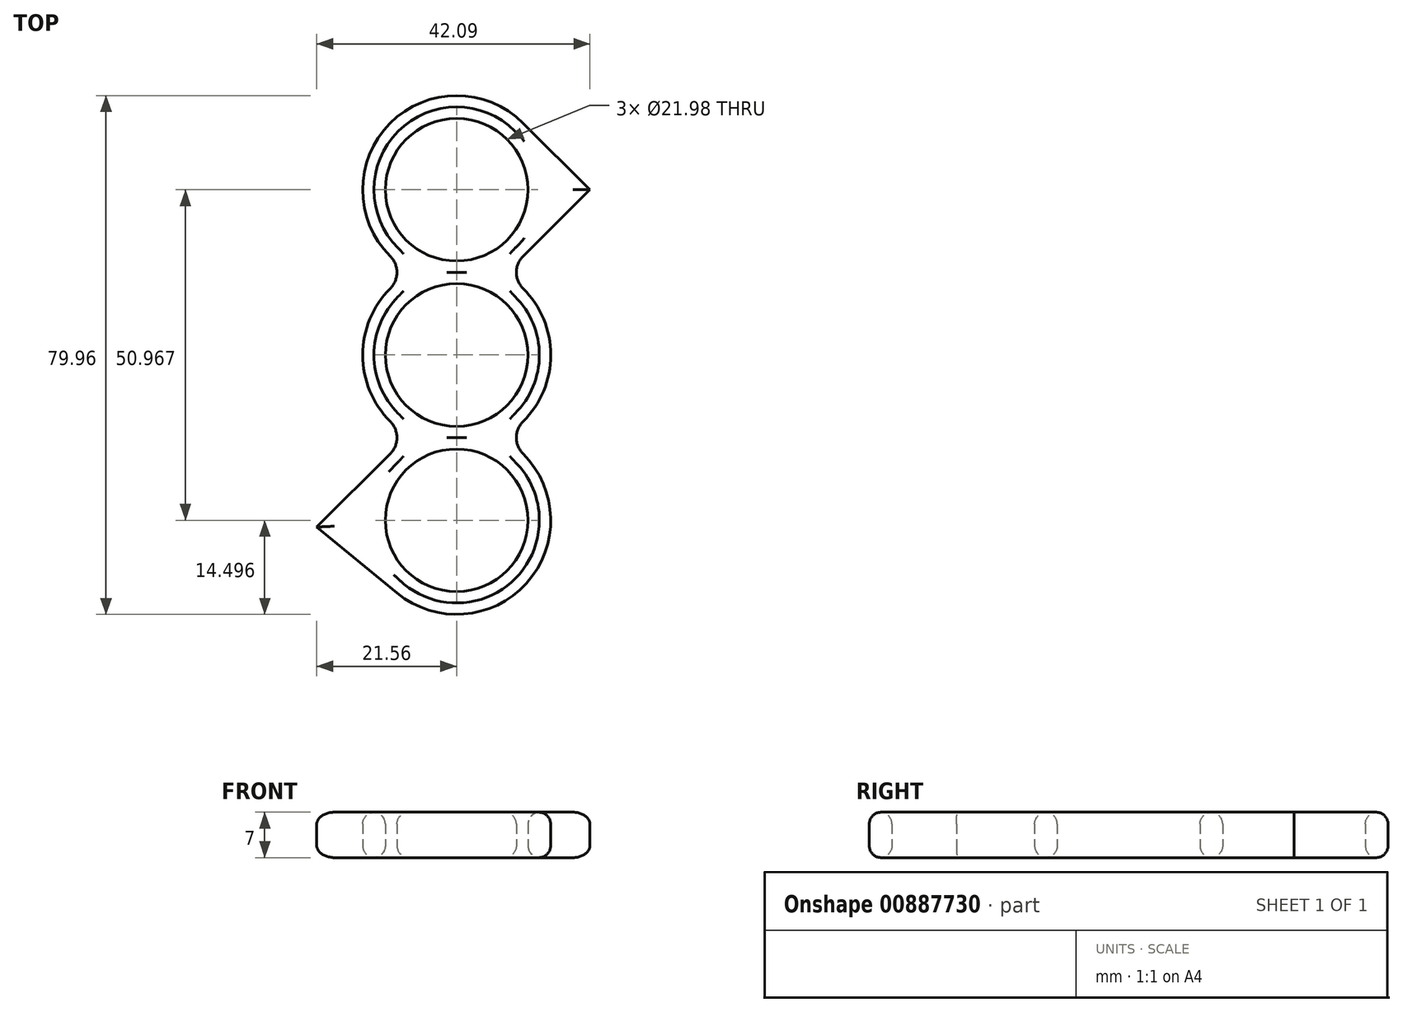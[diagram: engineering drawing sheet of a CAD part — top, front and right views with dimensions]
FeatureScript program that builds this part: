
annotation { "Feature Type Name" : "Feature", "Feature Type Description" : "" }
export const myFeature = defineFeature(function(context is Context, id is Id, definition is map)
    precondition{}
    {
        {
            var Q0;
            Q0=qCreatedBy(makeId("Top.planeOp"),FACE);
            var sketch = newSketch(context, id + "F0", { "sketchPlane" : qUnion([Q0])});
            skCircle(sketch, "E0", {"center": v(0, 0) * mm, "radius": 11 * mm});
            skCircle(sketch, "E1", {"center": v(0, 25.48) * mm, "radius": 11 * mm});
            skCircle(sketch, "E2", {"center": v(0, -25.48) * mm, "radius": 11 * mm});
            skLineSegment(sketch, "E3", {"start": v(0, 25.48) * mm, "end": v(0, -25.48) * mm, "construction": true});
            skLineSegment(sketch, "E4.bottom", {"start": v(-29.85, 57.15) * mm, "end": v(29.85, 57.15) * mm, "construction": true});
            skLineSegment(sketch, "E4.top", {"start": v(-29.85, -57.15) * mm, "end": v(29.85, -57.15) * mm, "construction": true});
            skLineSegment(sketch, "E4.left", {"start": v(-29.84, 57.15) * mm, "end": v(-29.85, -57.15) * mm, "construction": true});
            skLineSegment(sketch, "E4.right", {"start": v(29.85, 57.15) * mm, "end": v(29.84, -57.15) * mm, "construction": true});
            skPoint(sketch, "E5", {"position": v(0, 57.15) * mm});
            skPoint(sketch, "E6", {"position": v(-29.85, 0) * mm});
            skSolve(sketch);
        }
        {
            var Q0;
            Q0=qCreatedBy(makeId("Top.planeOp"),FACE);
            var sketch = newSketch(context, id + "F1", { "sketchPlane" : qUnion([Q0])});
            skCircle(sketch, "E7", {"center": v(0, 25.48) * mm, "radius": 11 * mm});
            skCircle(sketch, "E8", {"center": v(0, 0) * mm, "radius": 11 * mm});
            skCircle(sketch, "E9", {"center": v(0, -25.48) * mm, "radius": 11 * mm});
            skLineSegment(sketch, "E10.bottom", {"start": v(-29.85, 57.15) * mm, "end": v(29.84, 57.15) * mm, "construction": true});
            skLineSegment(sketch, "E10.top", {"start": v(-29.85, -57.15) * mm, "end": v(29.84, -57.15) * mm, "construction": true});
            skLineSegment(sketch, "E10.left", {"start": v(-29.85, 57.15) * mm, "end": v(-29.85, -57.15) * mm, "construction": true});
            skLineSegment(sketch, "E10.right", {"start": v(29.85, 57.15) * mm, "end": v(29.85, -57.15) * mm, "construction": true});
            skPoint(sketch, "E11", {"position": v(-29.85, 0) * mm});
            skPoint(sketch, "E12", {"position": v(0, 57.15) * mm});
            skArc(sketch, "E13.0", {"start": v(10.23, 35.75) * mm, "mid": v(-10.26, 35.72) * mm, "end": v(-10.23, 15.22) * mm});
            skArc(sketch, "E14.0", {"start": v(-10.23, 10.26) * mm, "mid": v(-14.5, 0) * mm, "end": v(-10.23, -10.26) * mm});
            skArc(sketch, "E15.0", {"start": v(-9.2, -36.68) * mm, "mid": v(10.74, -35.21) * mm, "end": v(10.23, -15.22) * mm});
            skArc(sketch, "E16.trimOffspring", {"start": v(10.23, -10.26) * mm, "mid": v(14.5, 0) * mm, "end": v(10.23, 10.26) * mm});
            skPoint(sketch, "E17.visualSharp", {"position": v(-6.9, 12.74) * mm});
            skArc(sketch, "E17.filletArc", {"start": v(-10.23, 10.26) * mm, "mid": v(-9.2, 12.74) * mm, "end": v(-10.23, 15.22) * mm});
            skPoint(sketch, "E18.visualSharp", {"position": v(6.9, 12.74) * mm});
            skArc(sketch, "E18.filletArc", {"start": v(10.23, 15.22) * mm, "mid": v(9.2, 12.74) * mm, "end": v(10.23, 10.26) * mm});
            skPoint(sketch, "E19.visualSharp", {"position": v(6.9, -12.74) * mm});
            skArc(sketch, "E19.filletArc", {"start": v(10.23, -10.26) * mm, "mid": v(9.2, -12.74) * mm, "end": v(10.23, -15.22) * mm});
            skPoint(sketch, "E20.visualSharp", {"position": v(-6.9, -12.74) * mm});
            skArc(sketch, "E20.filletArc", {"start": v(-10.23, -15.22) * mm, "mid": v(-9.2, -12.74) * mm, "end": v(-10.23, -10.26) * mm});
            skPoint(sketch, "E21.end.orphan", {"position": v(10.23, 35.75) * mm});
            skLineSegment(sketch, "E22", {"start": v(10.23, 35.75) * mm, "end": v(20.53, 25.48) * mm});
            skLineSegment(sketch, "E23", {"start": v(-9.2, -36.68) * mm, "end": v(-21.56, -26.52) * mm});
            skPoint(sketch, "E23.startSnap0", {"position": v(-9.2, -12.74) * mm});
            skLineSegment(sketch, "E24", {"start": v(-10.23, -15.22) * mm, "end": v(-21.56, -26.52) * mm});
            skLineSegment(sketch, "E25", {"start": v(10.23, 15.22) * mm, "end": v(20.53, 25.48) * mm});
            skSolve(sketch);
        }
        {
            var Q0;
            Q0=qSketchRegion(id+"F1",true);
            extrude(context, id + "F2", {"entities" : qUnion([Q0]), "depth" : 7 * mm, "offsetDistance" : 25.4 * mm});
        }
        {
            var Q0;
            Q0=makeQuery(id+"F2.opExtrude","CAP_EDGE",EDGE,{"disambiguationData":[OSD([sQuery(id+"F1.wireOp",EDGE,"E15.0")])],"isStart":false});
            var Q1;
            Q1=makeQuery(id+"F2.opExtrude","CAP_FACE",FACE,{"disambiguationData":[OSD([sQuery(id+"F1.wireOp",EDGE,"E7"),sQuery(id+"F1.wireOp",EDGE,"E8"),sQuery(id+"F1.wireOp",EDGE,"E9"),sQuery(id+"F1.wireOp",EDGE,"E13.0"),sQuery(id+"F1.wireOp",EDGE,"E14.0"),sQuery(id+"F1.wireOp",EDGE,"E15.0"),sQuery(id+"F1.wireOp",EDGE,"E16.trimOffspring"),sQuery(id+"F1.wireOp",EDGE,"E17.filletArc"),sQuery(id+"F1.wireOp",EDGE,"E18.filletArc"),sQuery(id+"F1.wireOp",EDGE,"E19.filletArc"),sQuery(id+"F1.wireOp",EDGE,"E20.filletArc"),sQuery(id+"F1.wireOp",EDGE,"E22"),sQuery(id+"F1.wireOp",EDGE,"E23"),sQuery(id+"F1.wireOp",EDGE,"E24"),sQuery(id+"F1.wireOp",EDGE,"E25")])],"isStart":false});
            var Q2;
            Q2=makeQuery(id+"F2.opExtrude","CAP_FACE",FACE,{"disambiguationData":[OSD([sQuery(id+"F1.wireOp",EDGE,"E7"),sQuery(id+"F1.wireOp",EDGE,"E8"),sQuery(id+"F1.wireOp",EDGE,"E9"),sQuery(id+"F1.wireOp",EDGE,"E13.0"),sQuery(id+"F1.wireOp",EDGE,"E14.0"),sQuery(id+"F1.wireOp",EDGE,"E15.0"),sQuery(id+"F1.wireOp",EDGE,"E16.trimOffspring"),sQuery(id+"F1.wireOp",EDGE,"E17.filletArc"),sQuery(id+"F1.wireOp",EDGE,"E18.filletArc"),sQuery(id+"F1.wireOp",EDGE,"E19.filletArc"),sQuery(id+"F1.wireOp",EDGE,"E20.filletArc"),sQuery(id+"F1.wireOp",EDGE,"E22"),sQuery(id+"F1.wireOp",EDGE,"E23"),sQuery(id+"F1.wireOp",EDGE,"E24"),sQuery(id+"F1.wireOp",EDGE,"E25")])],"isStart":true});
            fillet(context, id + "F3", {"entities" : qUnion([Q0, Q1, Q2]), "radius" : 1.84 * mm, "tangentPropagation" : true, "allowEdgeOverflow" : false});
        }
    });
